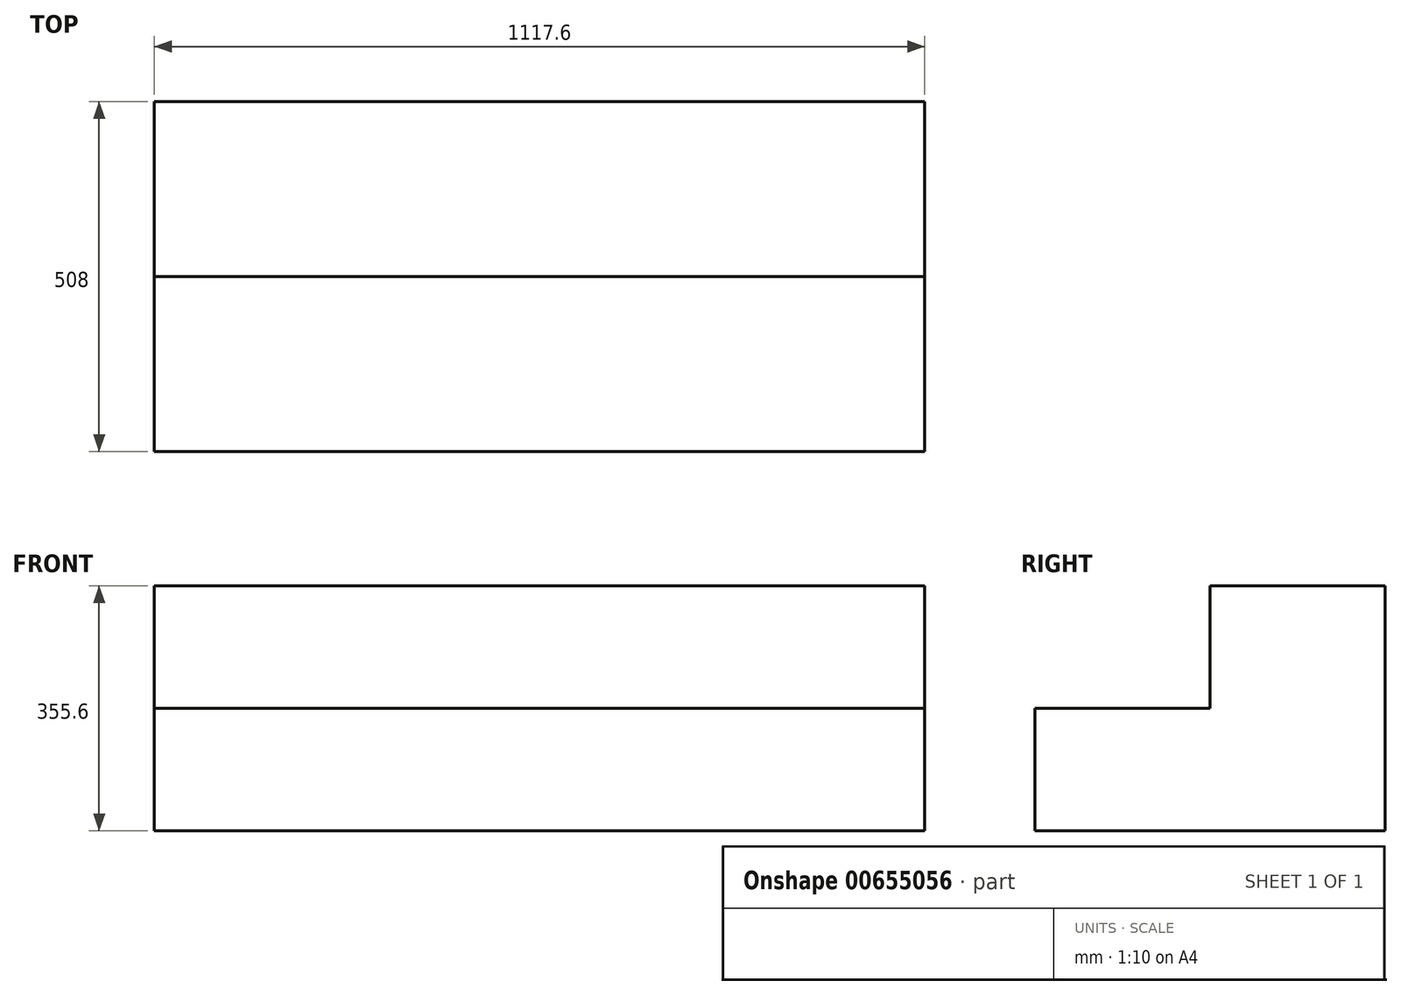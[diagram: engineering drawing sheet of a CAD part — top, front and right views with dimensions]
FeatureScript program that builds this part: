
annotation { "Feature Type Name" : "Feature", "Feature Type Description" : "" }
export const myFeature = defineFeature(function(context is Context, id is Id, definition is map)
    precondition{}
    {
        {
            var Q0;
            Q0=qCreatedBy(makeId("Right.planeOp"),FACE);
            var sketch = newSketch(context, id + "F0", { "sketchPlane" : qUnion([Q0])});
            skLineSegment(sketch, "E0", {"start": v(0, 0) * mm, "end": v(0, 355.6) * mm});
            skLineSegment(sketch, "E1", {"start": v(0, 355.6) * mm, "end": v(-254, 355.6) * mm});
            skLineSegment(sketch, "E2", {"start": v(-254, 355.6) * mm, "end": v(-254, 177.8) * mm});
            skLineSegment(sketch, "E3", {"start": v(-254, 177.8) * mm, "end": v(-508, 177.8) * mm});
            skLineSegment(sketch, "E4", {"start": v(-508, 177.8) * mm, "end": v(-508, 0) * mm});
            skLineSegment(sketch, "E5", {"start": v(-508, 0) * mm, "end": v(0, 0) * mm});
            skSolve(sketch);
        }
        {
            var Q0;
            Q0=makeQuery(id+"F0.imprint","IMPRINT",FACE,{"disambiguationData":[TD([[makeQuery(id+"F0.imprint","IMPRINT",EDGE,{"derivedFrom":sQuery(id+"F0.wireOp",EDGE,"E0")}),1.0]])]});
            extrude(context, id + "F1", {"entities" : qUnion([Q0]), "depth" : 1117.6 * mm, "offsetDistance" : 25.4 * mm});
        }
    });
